# Revit family: Gripple Brackets with UniGrip Suspensions - Assembly
name_source: partatom
category: Specialty Equipment
revit_build: Autodesk Revit 2017 (Build: 20160225_1515(x64)
units: mm (PartAtom-declared; Revit-internal decimal feet)

## family parameters
Always vertical = Yes
Cut with Voids When Loaded = Yes
Part Type = Normal
Room Calculation Point = No
Round Connector Dimension = Use Diameter
Shared = Yes
Work Plane-Based = Yes

## types (14) — shared parameters
Manufacturer = Gripple Ltd
URL = http://www.gripple.co.uk
zero-valued in all types: Default Elevation

## per-type parameters (varying)
| type | +L | -L | Bracket | Length |
| PB1540 | 770 mm  [stored 2.52625 ft] | -770 mm  [stored -2.52625 ft] | Gripple Brackets : PB1540 | 1540 mm |
| PB1440 | 720 mm  [stored 2.3622 ft] | -720 mm  [stored -2.3622 ft] | Gripple Brackets : PB1440 | 1440 mm |
| PB1340 | 670 mm  [stored 2.19816 ft] | -670 mm  [stored -2.19816 ft] | Gripple Brackets : PB1340 | 1340 mm |
| PB440 | 220 mm  [stored 0.721785 ft] | -220 mm  [stored -0.721785 ft] | Gripple Brackets : PB440 | 440 mm  [stored 1.44357 ft] |
| PB540 | 270 mm  [stored 0.885827 ft] | -270 mm  [stored -0.885827 ft] | Gripple Brackets : PB540 | 540 mm  [stored 1.77165 ft] |
| PB740 | 370 mm  [stored 1.21391 ft] | -370 mm  [stored -1.21391 ft] | Gripple Brackets : PB740 | 740 mm  [stored 2.42782 ft] |
| PB940 | 470 mm  [stored 1.54199 ft] | -470 mm  [stored -1.54199 ft] | Gripple Brackets : PB940 | 940 mm  [stored 3.08399 ft] |
| PB1040 | 520 mm  [stored 1.70604 ft] | -520 mm  [stored -1.70604 ft] | Gripple Brackets : PB1040 | 1040 mm  [stored 3.41207 ft] |
| PB1140 | 570 mm  [stored 1.87008 ft] | -570 mm  [stored -1.87008 ft] | Gripple Brackets : PB1140 | 1140 mm  [stored 3.74016 ft] |
| PB1240 | 620 mm  [stored 2.03412 ft] | -620 mm  [stored -2.03412 ft] | Gripple Brackets : PB1240 | 1240 mm  [stored 4.06824 ft] |
| PB340 | 170 mm  [stored 0.557743 ft] | -170 mm  [stored -0.557743 ft] | Gripple Brackets : PB340 | 340 mm  [stored 1.11549 ft] |
| PB840 | 420 mm  [stored 1.37795 ft] | -420 mm  [stored -1.37795 ft] | Gripple Brackets : PB840 | 840 mm  [stored 2.75591 ft] |
| PB240 | 120 mm  [stored 0.393701 ft] | -120 mm  [stored -0.393701 ft] | Gripple Brackets : PB240 | 240 mm  [stored 0.787402 ft] |
| PB640 | 320 mm  [stored 1.04987 ft] | -320 mm  [stored -1.04987 ft] | Gripple Brackets : PB640 | 640 mm  [stored 2.09974 ft] |

note: column(s) folded — value = type name in every type: Assembly Code, Model

note: [stored X ft] marks values corroborated as IEEE doubles in the binary element streams (Revit-internal decimal feet)

## geometry (parser evidence)
native form markers: Sweep x18
no freeform markers — native parametric forms only
